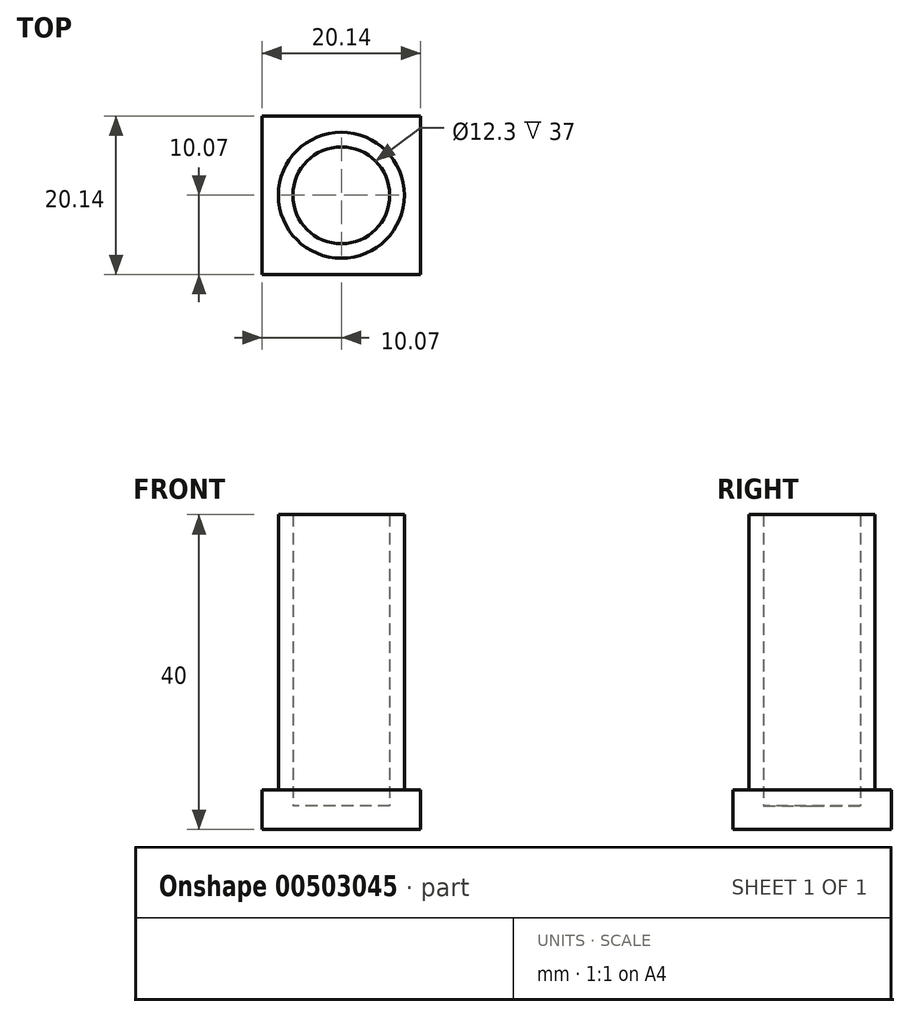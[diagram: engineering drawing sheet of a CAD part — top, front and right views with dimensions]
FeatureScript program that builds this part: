
annotation { "Feature Type Name" : "Feature", "Feature Type Description" : "" }
export const myFeature = defineFeature(function(context is Context, id is Id, definition is map)
    precondition{}
    {
        {
            var Q0;
            Q0=qCreatedBy(makeId("Top.planeOp"),FACE);
            var sketch = newSketch(context, id + "F0", { "sketchPlane" : qUnion([Q0])});
            skCircle(sketch, "E0", {"center": v(0, 0) * mm, "radius": 6.15 * mm});
            skCircle(sketch, "E1", {"center": v(0, 0) * mm, "radius": 8 * mm});
            skLineSegment(sketch, "E2.bottom", {"start": v(10.07, -10.07) * mm, "end": v(-10.07, -10.07) * mm});
            skLineSegment(sketch, "E2.top", {"start": v(10.07, 10.07) * mm, "end": v(-10.07, 10.07) * mm});
            skLineSegment(sketch, "E2.left", {"start": v(10.07, -10.07) * mm, "end": v(10.07, 10.07) * mm});
            skLineSegment(sketch, "E2.right", {"start": v(-10.07, -10.07) * mm, "end": v(-10.07, 10.07) * mm});
            skSolve(sketch);
        }
        {
            var Q0;
            Q0 = qSketchRegion(id + "F0", true);
            extrude(context, id + "F1", {"entities" : qUnion([Q0]), "depth" : 5 * mm});
        }
        {
            var Q0;
            Q0=makeQuery(id+"F0.imprint","IMPRINT",FACE,{"disambiguationData":[TD([[makeQuery(id+"F0.imprint","IMPRINT",EDGE,{"derivedFrom":sQuery(id+"F0.wireOp",EDGE,"E0")}),-1.0]])]});
            extrude(context, id + "F2", {"entities" : qUnion([Q0]), "operationType" : NewBodyOperationType.ADD, "depth" : 40 * mm});
        }
        {
            var Q0;
            Q0=makeQuery(id+"F0.imprint","IMPRINT",FACE,{"disambiguationData":[TD([[makeQuery(id+"F0.imprint","IMPRINT",EDGE,{"derivedFrom":sQuery(id+"F0.wireOp",EDGE,"E0")}),1.0]])]});
            extrude(context, id + "F3", {"entities" : qUnion([Q0]), "operationType" : NewBodyOperationType.ADD, "depth" : 3 * mm});
        }
    });
